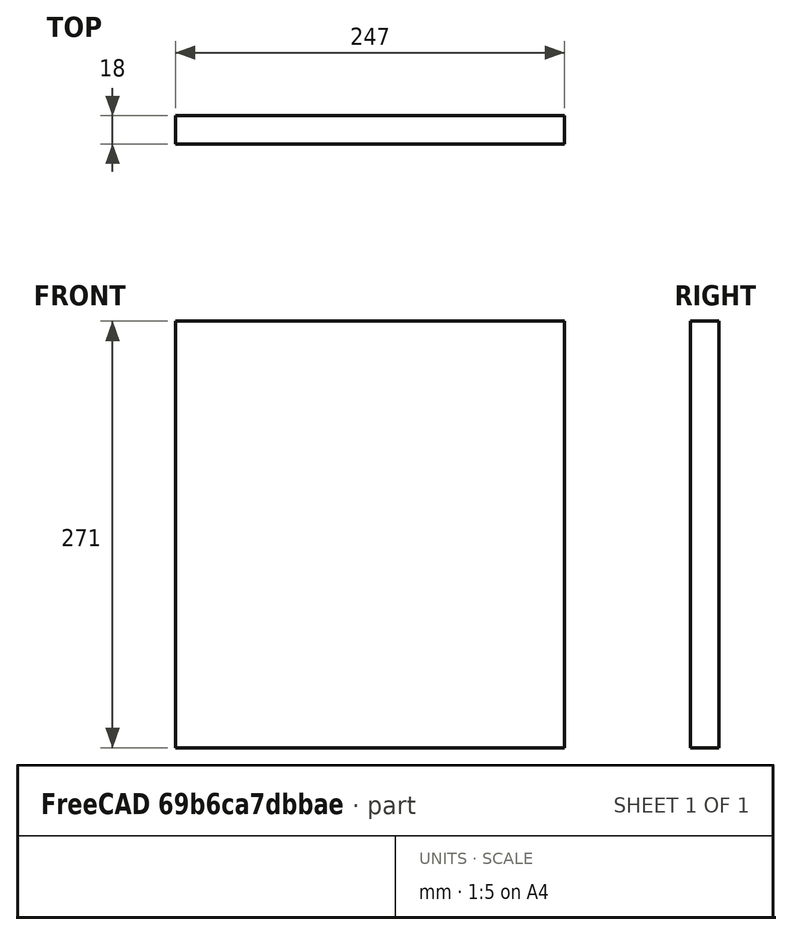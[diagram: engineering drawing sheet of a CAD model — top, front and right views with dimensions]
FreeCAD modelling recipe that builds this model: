
FCSTD DOCUMENT  (FreeCAD 0.18R4 (GitTag))
Label: back
License: All rights reserved
LicenseURL: http://en.wikipedia.org/wiki/All_rights_reserved
objects: Sketcher::SketchObject×1, PartDesign::Pad×1, PartDesign::Body×1
note: 4 computed .brp shape members not serialized (recipe doc carries the construction recipe); baked Part::Feature solids carry a one-line shape summary decoded from their .brp

FEATURE [Sketcher::SketchObject] Sketch
  MapMode = 5
  Placement = pos=(0,0,0) rot=(1,0,0;1.5708rad)
  Support = -> [XZ_Plane]
  sketch-geometry (4):
    g0: LineSegment StartX=0 StartY=0 StartZ=0 EndX=-247 EndY=0 EndZ=0
    g1: LineSegment StartX=-247 StartY=0 StartZ=0 EndX=-247 EndY=271 EndZ=0
    g2: LineSegment StartX=-247 StartY=271 StartZ=0 EndX=0 EndY=271 EndZ=0
    g3: LineSegment StartX=0 StartY=271 StartZ=0 EndX=0 EndY=0 EndZ=0
  constraints (11):
    c: Coincident(g0,g1)
    c: Coincident(g1,g2)
    c: Coincident(g2,g3)
    c: Coincident(g3,g0)
    c: Horizontal(g0)
    c: Horizontal(g2)
    c: Vertical(g1)
    c: Vertical(g3)
    c: Coincident(g0,g-1)
    c: DistanceX(g0,g0) = 247
    c: DistanceY(g3,g3) = 271
FEATURE [PartDesign::Pad] Pad
  Length = 18
  Length2 = 100
  Placement = pos=(0,0,0) rot=(1,0,0;1.5708rad)
  Profile = -> Sketch
  Type = 0
FEATURE [PartDesign::Body] Body
  Group = -> [Sketch,Pad]
  Origin = -> Origin
  Tip = -> Pad
